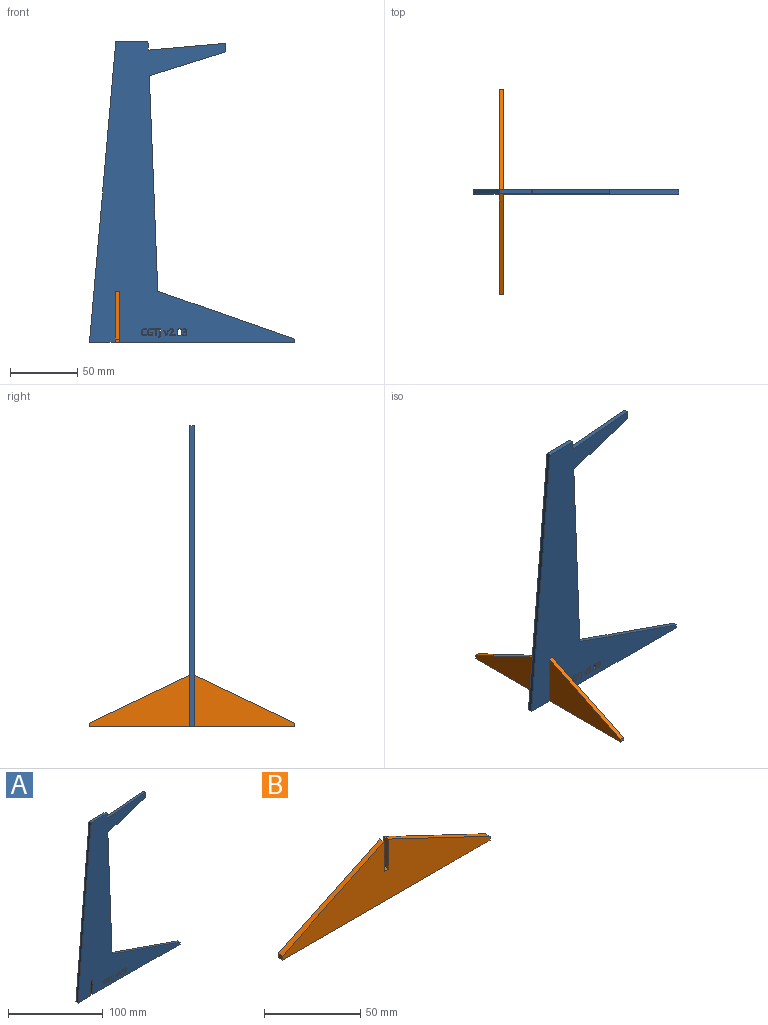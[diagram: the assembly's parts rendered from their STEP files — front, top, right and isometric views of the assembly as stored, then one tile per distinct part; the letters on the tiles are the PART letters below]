
ASSEMBLY  parts=2 mates=1
PART A: 143 faces, bbox 152.4x3.2x223.6 mm
  f0: extruded ~3.18x1.14mm, area 3.8mm2, adj f1,f140,f141,f142
  f1: extruded ~3.18x1.31mm, area 4.7mm2, adj f0,f2,f141,f142
  f2: extruded ~3.18x1.51mm, area 5.2mm2, adj f1,f3,f141,f142
  f3: extruded ~3.18x1.53mm, area 5.2mm2, adj f2,f4,f141,f142
  f4: extruded ~3.18x1.32mm, area 4.7mm2, adj f3,f5,f141,f142
  f5: extruded ~3.18x1.2mm, area 3.9mm2, adj f4,f6,f141,f142
  f6: plane 3.18x0.51mm, normal (-1,0,0), area 1.6mm2, adj f5,f7,f141,f142
  f7: extruded ~3.18x1.29mm, area 4.2mm2, adj f6,f8,f141,f142
  f8: extruded ~3.18x1.72mm, area 6mm2, adj f7,f9,f141,f142
  f9: extruded ~3.18x1.92mm, area 6.5mm2, adj f8,f10,f141,f142
  f10: extruded ~3.18x1.36mm, area 4.5mm2, adj f9,f11,f141,f142
  f11: extruded ~3.18x0.9mm, area 4mm2, adj f10,f12,f141,f142
  f12: extruded ~3.18x1.29mm, area 4.3mm2, adj f11,f13,f141,f142
  f13: extruded ~3.18x1.38mm, area 4.5mm2, adj f12,f140,f141,f142
  f14: plane 3.18x0.52mm, normal (1,0,0), area 1.7mm2, adj f15,f131,f141,f142
  f15: plane 3.18x1.71mm, normal (0,0,-1), area 5.4mm2, adj f14,f16,f141,f142
  f16: plane 3.18x2.45mm, normal (-1,0,0), area 7.8mm2, adj f15,f17,f141,f142
  f17: extruded ~3.18x0.81mm, area 2.7mm2, adj f16,f18,f141,f142
  f18: extruded ~3.18x0.96mm, area 3.1mm2, adj f17,f19,f141,f142
  f19: extruded ~3.18x1.78mm, area 6.2mm2, adj f18,f20,f141,f142
  f20: extruded ~3.18x1.91mm, area 6.5mm2, adj f19,f21,f141,f142
  f21: extruded ~3.18x1.38mm, area 4.5mm2, adj f20,f22,f141,f142
  f22: extruded ~3.18x0.91mm, area 4.1mm2, adj f21,f23,f141,f142
  f23: extruded ~3.18x1.39mm, area 4.6mm2, adj f22,f24,f141,f142
  f24: extruded ~3.18x1.5mm, area 4.9mm2, adj f23,f25,f141,f142
  f25: plane 3.18x0.52mm, normal (-0.92,0,0.4), area 1.8mm2, adj f24,f26,f141,f142
  f26: extruded ~3.18x1.31mm, area 4.3mm2, adj f25,f27,f141,f142
  f27: extruded ~3.18x1.44mm, area 5mm2, adj f26,f28,f141,f142
  f28: extruded ~3.18x1.52mm, area 5.2mm2, adj f27,f29,f141,f142
  f29: extruded ~3.18x1.55mm, area 5.3mm2, adj f28,f30,f141,f142
  f30: extruded ~3.18x1.46mm, area 5.1mm2, adj f29,f31,f141,f142
  f31: extruded ~3.18x1.02mm, area 3.3mm2, adj f30,f32,f141,f142
  f32: plane 3.18x1.55mm, normal (1,0,0), area 4.9mm2, adj f31,f131,f141,f142
  f33: plane 4.52x3.18mm, normal (-1,0,0), area 14.3mm2, adj f34,f132,f141,f142
  f34: plane 3.18x0.59mm, normal (0,0,1), area 1.9mm2, adj f33,f35,f141,f142
  f35: plane 4.52x3.18mm, normal (1,0,0), area 14.3mm2, adj f34,f36,f141,f142
  f36: plane 3.18x1.6mm, normal (0,0,1), area 5.1mm2, adj f35,f37,f141,f142
  f37: plane 3.18x0.52mm, normal (1,0,0), area 1.7mm2, adj f36,f38,f141,f142
  f38: plane 3.78x3.18mm, normal (0,0,-1), area 12mm2, adj f37,f39,f141,f142
  f39: plane 3.18x0.52mm, normal (-1,0,0), area 1.7mm2, adj f38,f132,f141,f142
  f40: extruded ~3.18x0.95mm, area 3.3mm2, adj f41,f133,f141,f142
  f41: extruded ~3.18x0.51mm, area 1.7mm2, adj f40,f42,f141,f142
  f42: plane 3.18x0.5mm, normal (1,0,0), area 1.6mm2, adj f41,f43,f141,f142
  f43: extruded ~3.18x0.51mm, area 1.6mm2, adj f42,f44,f141,f142
  f44: extruded ~3.18x0.52mm, area 1.8mm2, adj f43,f45,f141,f142
  f45: extruded ~3.18x0.6mm, area 2mm2, adj f44,f46,f141,f142
  f46: plane 5.04x3.18mm, normal (1,0,0), area 16mm2, adj f45,f47,f141,f142
  f47: plane 3.18x0.59mm, normal (0,0,-1), area 1.9mm2, adj f46,f48,f141,f142
  f48: plane 4.99x3.18mm, normal (-1,0,0), area 15.8mm2, adj f47,f133,f141,f142
  f49: plane 3.18x0.67mm, normal (0,0,1), area 2.1mm2, adj f50,f134,f141,f142
  f50: plane 3.78x3.18mm, normal (0.93,0,0.35), area 12.8mm2, adj f49,f51,f141,f142
  f51: plane 3.18x0.61mm, normal (0,0,-1), area 1.9mm2, adj f50,f52,f141,f142
  f52: plane 3.18x2.24mm, normal (-0.94,0,-0.34), area 7.6mm2, adj f51,f53,f141,f142
  f53: extruded ~3.18x1.02mm, area 3.4mm2, adj f52,f54,f141,f142
  f54: plane 3.18x0.03mm, normal (0,0,-1), area 0.1mm2, adj f53,f55,f141,f142
  f55: extruded ~3.18x0.76mm, area 2.5mm2, adj f54,f56,f141,f142
  f56: extruded ~3.18x2.5mm, area 8.4mm2, adj f55,f57,f141,f142
  f57: plane 3.18x0.61mm, normal (0,0,-1), area 1.9mm2, adj f56,f134,f141,f142
  f58: plane 3.18x0.53mm, normal (-1,0,0), area 1.7mm2, adj f59,f135,f141,f142
  f59: plane 3.31x3.18mm, normal (0,0,1), area 10.5mm2, adj f58,f60,f141,f142
  f60: plane 3.18x0.49mm, normal (1,0,0), area 1.6mm2, adj f59,f61,f141,f142
  f61: plane 3.18x1.33mm, normal (0.71,0,-0.71), area 6mm2, adj f60,f62,f141,f142
  f62: extruded ~3.18x0.88mm, area 3.8mm2, adj f61,f63,f141,f142
  f63: extruded ~3.18x0.51mm, area 1.9mm2, adj f62,f64,f141,f142
  f64: extruded ~3.18x0.53mm, area 1.7mm2, adj f63,f65,f141,f142
  f65: extruded ~3.18x0.64mm, area 2.2mm2, adj f64,f66,f141,f142
  f66: extruded ~3.18x0.68mm, area 2.3mm2, adj f65,f67,f141,f142
  f67: extruded ~3.18x0.59mm, area 1.9mm2, adj f66,f68,f141,f142
  f68: extruded ~3.18x0.63mm, area 2.3mm2, adj f67,f69,f141,f142
  f69: plane 3.18x0.39mm, normal (0.79,0,0.61), area 1.6mm2, adj f68,f70,f141,f142
  f70: extruded ~3.18x1.52mm, area 5.3mm2, adj f69,f71,f141,f142
  f71: extruded ~3.18x1.11mm, area 3.8mm2, adj f70,f72,f141,f142
  f72: extruded ~3.18x0.98mm, area 3.5mm2, adj f71,f73,f141,f142
  f73: extruded ~3.18x0.95mm, area 3.2mm2, adj f72,f74,f141,f142
  f74: extruded ~3.18x1.19mm, area 4.9mm2, adj f73,f75,f141,f142
  f75: plane 3.18x1.1mm, normal (-0.7,0,0.71), area 4.9mm2, adj f74,f76,f141,f142
  f76: plane 3.18x0.03mm, normal (-1,0,0), area 0.1mm2, adj f75,f135,f141,f142
  f77: extruded ~3.18x0.36mm, area 1.2mm2, adj f78,f136,f141,f142
  f78: extruded ~3.18x0.35mm, area 1.2mm2, adj f77,f79,f141,f142
  f79: extruded ~3.18x0.3mm, area 1.1mm2, adj f78,f80,f141,f142
  f80: extruded ~3.18x0.31mm, area 1.1mm2, adj f79,f81,f141,f142
  f81: extruded ~3.18x0.35mm, area 1.2mm2, adj f80,f82,f141,f142
  f82: extruded ~3.18x0.34mm, area 1.2mm2, adj f81,f83,f141,f142
  f83: extruded ~3.18x0.31mm, area 1.1mm2, adj f82,f136,f141,f142
  f84: extruded ~3.18x1.93mm, area 6.3mm2, adj f85,f137,f141,f142
  f85: extruded ~3.18x1.95mm, area 6.4mm2, adj f84,f86,f141,f142
  f86: extruded ~3.18x1.26mm, area 4.7mm2, adj f85,f87,f141,f142
  f87: extruded ~3.18x1.24mm, area 4.7mm2, adj f86,f88,f141,f142
  f88: extruded ~3.18x1.94mm, area 6.4mm2, adj f87,f89,f141,f142
  f89: extruded ~3.18x1.95mm, area 6.4mm2, adj f88,f90,f141,f142
  f90: extruded ~3.18x1.25mm, area 4.7mm2, adj f89,f137,f141,f142
  f91: extruded ~3.18x0.92mm, area 3.3mm2, adj f92,f138,f141,f142
  f92: extruded ~3.18x0.79mm, area 2.7mm2, adj f91,f93,f141,f142
  f93: extruded ~3.18x0.77mm, area 2.8mm2, adj f92,f94,f141,f142
  f94: plane 3.18x0.03mm, normal (-1,0,0), area 0.1mm2, adj f93,f95,f141,f142
  f95: extruded ~3.18x0.9mm, area 3.2mm2, adj f94,f96,f141,f142
  f96: extruded ~3.18x0.81mm, area 2.8mm2, adj f95,f97,f141,f142
  f97: extruded ~3.18x1.11mm, area 4mm2, adj f96,f98,f141,f142
  f98: extruded ~3.18x1.42mm, area 4.8mm2, adj f97,f99,f141,f142
  f99: extruded ~3.18x0.73mm, area 2.3mm2, adj f98,f100,f141,f142
  f100: extruded ~3.18x0.65mm, area 2.2mm2, adj f99,f101,f141,f142
  f101: plane 3.18x0.54mm, normal (1,0,0), area 1.7mm2, adj f100,f102,f141,f142
  f102: extruded ~3.18x0.7mm, area 2.4mm2, adj f101,f103,f141,f142
  f103: extruded ~3.18x0.7mm, area 2.2mm2, adj f102,f104,f141,f142
  f104: extruded ~3.18x1.31mm, area 6mm2, adj f103,f105,f141,f142
  f105: extruded ~3.18x1.44mm, area 6.1mm2, adj f104,f106,f141,f142
  f106: plane 3.18x0.5mm, normal (0,0,1), area 1.6mm2, adj f105,f107,f141,f142
  f107: plane 3.18x0.49mm, normal (1,0,0), area 1.6mm2, adj f106,f108,f141,f142
  f108: plane 3.18x0.5mm, normal (0,0,-1), area 1.6mm2, adj f107,f109,f141,f142
  f109: extruded ~3.18x0.93mm, area 3.1mm2, adj f108,f110,f141,f142
  f110: extruded ~3.18x0.72mm, area 2.6mm2, adj f109,f111,f141,f142
  f111: extruded ~3.18x0.58mm, area 2.1mm2, adj f110,f112,f141,f142
  f112: extruded ~3.18x0.69mm, area 2.3mm2, adj f111,f113,f141,f142
  f113: extruded ~3.18x0.62mm, area 2mm2, adj f112,f114,f141,f142
  f114: extruded ~3.18x0.67mm, area 2.4mm2, adj f113,f115,f141,f142
  f115: plane 3.18x0.39mm, normal (0.8,0,0.6), area 1.5mm2, adj f114,f116,f141,f142
  f116: extruded ~3.18x0.71mm, area 2.6mm2, adj f115,f117,f141,f142
  f117: extruded ~3.18x0.85mm, area 2.8mm2, adj f116,f138,f141,f142
  f118: plane 223.61x19.56mm, normal (-1,0,0.09), area 712.7mm2, adj f119,f139,f141,f142
  f119: plane 19.05x3.18mm, normal (0,0,-1), area 60.5mm2, adj f118,f120,f141,f142
  f120: plane 19.05x3.18mm, normal (1,0,0), area 60.5mm2, adj f119,f121,f141,f142
  f121: plane 3.18x3.05mm, normal (0,0,-1), area 9.7mm2, adj f120,f122,f141,f142
  f122: plane 19.05x3.18mm, normal (-1,0,0), area 60.5mm2, adj f121,f123,f141,f142
  f123: plane 130.3x3.18mm, normal (0,0,-1), area 413.7mm2, adj f122,f124,f141,f142
  f124: plane 3.18x2.54mm, normal (1,0,0), area 8.1mm2, adj f123,f125,f141,f142
  f125: plane 101.6x35.56mm, normal (0.33,0,0.94), area 341.8mm2, adj f124,f126,f141,f142
  f126: plane 160.12x6.35mm, normal (1,0,0.04), area 508.8mm2, adj f125,f127,f141,f142
  f127: plane 56.6x17.7mm, normal (0.3,0,-0.95), area 188.3mm2, adj f126,f128,f141,f142
  f128: plane 6.35x3.18mm, normal (1,0,0), area 20.2mm2, adj f127,f129,f141,f142
  f129: plane 57.36x5.02mm, normal (-0.09,0,1), area 182.8mm2, adj f128,f130,f141,f142
  f130: plane 6.35x3.18mm, normal (1,0,0.04), area 20.2mm2, adj f129,f139,f141,f142
  f131: plane 3.18x1.13mm, normal (0,0,1), area 3.6mm2, adj f14,f32,f141,f142
  f132: plane 3.18x1.6mm, normal (0,0,1), area 5.1mm2, adj f33,f39,f141,f142
  f133: extruded ~3.18x1.01mm, area 3.5mm2, adj f40,f48,f141,f142
  f134: plane 3.78x3.18mm, normal (-0.93,0,0.35), area 12.8mm2, adj f49,f57,f141,f142
  f135: plane 3.18x2.59mm, normal (0,0,-1), area 8.2mm2, adj f58,f76,f141,f142
  f136: extruded ~3.18x0.29mm, area 1mm2, adj f77,f83,f141,f142
  f137: extruded ~3.18x1.25mm, area 4.7mm2, adj f84,f90,f141,f142
  f138: extruded ~3.18x1.14mm, area 3.8mm2, adj f91,f117,f141,f142
  f139: plane 23.88x3.18mm, normal (0,0,1), area 75.8mm2, adj f118,f130,f141,f142
  f140: plane 3.18x0.5mm, normal (-0.9,0,0.44), area 1.8mm2, adj f0,f13,f141,f142
  f141: plane 223.61x152.4mm, normal (0,-1,0), area 11170.8mm2, adj f0,f1,f2,f3,f4,f5,f6,f7
  f142: plane 223.61x152.4mm, normal (0,1,0), area 11170.8mm2, adj f0,f1,f2,f3,f4,f5,f6,f7
PART B: 10 faces, bbox 152.4x3.2x38.1 mm
  f0: plane 74.68x35.56mm, normal (-0.43,0,0.9), area 262.6mm2, adj f1,f7,f8,f9
  f1: plane 3.18x2.54mm, normal (-1,0,0), area 8.1mm2, adj f0,f2,f8,f9
  f2: plane 152.4x3.18mm, normal (0,0,-1), area 483.9mm2, adj f1,f3,f8,f9
  f3: plane 3.18x2.54mm, normal (1,0,0), area 8.1mm2, adj f2,f4,f8,f9
  f4: plane 74.68x35.56mm, normal (0.43,0,0.9), area 262.6mm2, adj f3,f5,f8,f9
  f5: plane 19.05x3.18mm, normal (-1,0,0), area 60.5mm2, adj f4,f6,f8,f9
  f6: plane 3.18x3.05mm, normal (0,0,1), area 9.7mm2, adj f5,f7,f8,f9
  f7: plane 19.05x3.18mm, normal (1,0,0), area 60.5mm2, adj f0,f6,f8,f9
  f8: plane 152.4x38.1mm, normal (0,-1,0), area 3092.9mm2, adj f0,f1,f2,f3,f4,f5,f6,f7
  f9: plane 152.4x38.1mm, normal (0,1,0), area 3092.9mm2, adj f0,f1,f2,f3,f4,f5,f6,f7
PLACE A t=(-159.82,24.92,-90.98)mm
PLACE B rot(axis=(0,0,-1),90deg) t=(-137.66,23.33,-90.98)mm
MATE fastened B.f6 <-> A.f121  axis (0,0,1) through (-139.24,23.33,-71.93)mm
